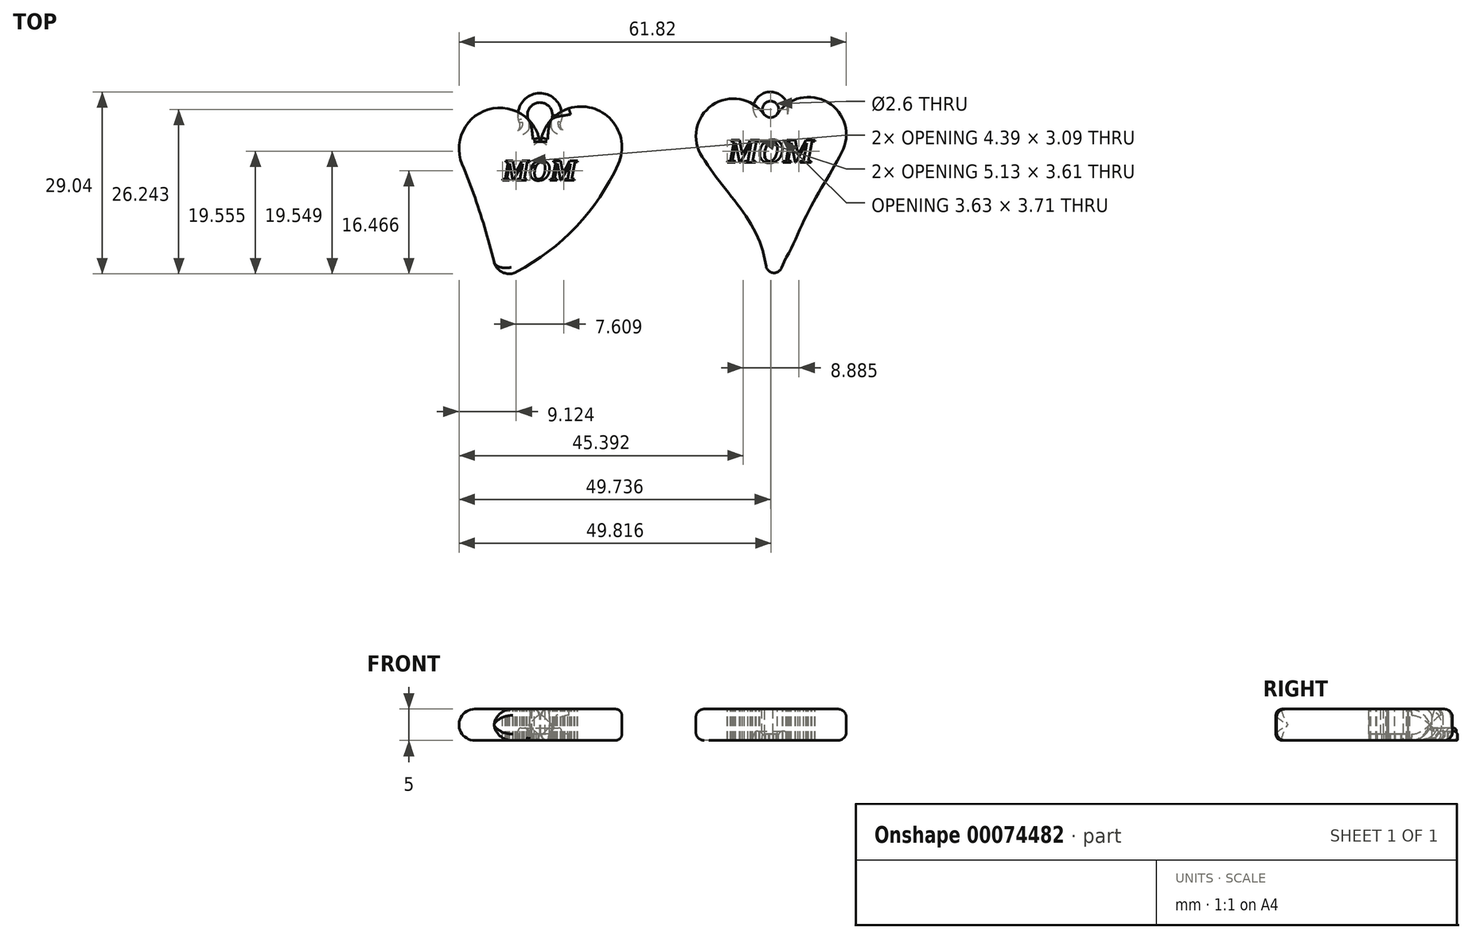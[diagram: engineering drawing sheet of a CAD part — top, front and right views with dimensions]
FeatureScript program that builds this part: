
annotation { "Feature Type Name" : "Feature", "Feature Type Description" : "" }
export const myFeature = defineFeature(function(context is Context, id is Id, definition is map)
    precondition{}
    {
        {
            var Q0;
            Q0=qCreatedBy(makeId("Top.planeOp"),FACE);
            var sketch = newSketch(context, id + "F0", { "sketchPlane" : qUnion([Q0])});
            skLineSegment(sketch, "E0.rect.bottom", {"start": v(-16, 20) * mm, "end": v(16, 20) * mm, "construction": true});
            skLineSegment(sketch, "E0.rect.top", {"start": v(-16, -20) * mm, "end": v(16, -20) * mm, "construction": true});
            skLineSegment(sketch, "E0.rect.left", {"start": v(-16, 20) * mm, "end": v(-16, -20) * mm, "construction": true});
            skLineSegment(sketch, "E0.rect.right", {"start": v(16, 20) * mm, "end": v(16, -20) * mm, "construction": true});
            skLineSegment(sketch, "E1", {"start": v(0, 0) * mm, "end": v(0, 20) * mm, "construction": true});
            skCircle(sketch, "E2", {"center": v(-6, 8.56) * mm, "radius": 6 * mm});
            skCircle(sketch, "E3", {"center": v(6, 8.8) * mm, "radius": 6 * mm});
            skFitSpline(sketch, "E4", {"points": [v(-11, 5.26) * mm, v(-8.06, 1.11) * mm, v(-4.05, -4.17) * mm, v(-1.25, -10.02) * mm, v(0, -13.64) * mm, v(2.4, -10.88) * mm, v(4.4, -6.78) * mm, v(5.94, -3.48) * mm, v(7.87, 0) * mm, v(8.52, 1.1) * mm, v(12.07, 7.48) * mm], "startDerivative": vector(36.89, -55.96) * mm, "endDerivative": vector(45.04, 87.27) * mm});
            skLineSegment(sketch, "E5", {"start": v(6, 8.8) * mm, "end": v(12, 8.8) * mm});
            skLineSegment(sketch, "E6", {"start": v(-1.28, -9.88) * mm, "end": v(0, -16.13) * mm});
            skLineSegment(sketch, "E7", {"start": v(0, -16.13) * mm, "end": v(2.4, -10.88) * mm});
            skSolve(sketch);
        }
        {
            var Q0;
            Q0 = qSketchRegion(id + "F0", true);
            extrude(context, id + "F1", {"entities" : qUnion([Q0]), "depth" : 5 * mm});
        }
        {
            var Q0;
            Q0=qCreatedBy(makeId("Top.planeOp"),FACE);
            var sketch = newSketch(context, id + "F2", { "sketchPlane" : qUnion([Q0])});
            skCircle(sketch, "E8", {"center": v(-43.32, 6.6) * mm, "radius": 6.5 * mm});
            skCircle(sketch, "E9", {"center": v(-30.32, 6.8) * mm, "radius": 6.5 * mm});
            skArc(sketch, "E10", {"start": v(-43.55, -14.49) * mm, "mid": v(-46.01, -5.06) * mm, "end": v(-49.32, 4.1) * mm});
            skArc(sketch, "E11", {"start": v(-43.55, -14.49) * mm, "mid": v(-32.21, -7) * mm, "end": v(-24.4, 4.1) * mm});
            skSolve(sketch);
        }
        {
            var Q0;
            {var subQ0=sQuery(id+"F2.wireOp",EDGE,"E10");Q0=makeQuery(id+"F2.imprint","IMPRINT",FACE,{"disambiguationData":[TD([[makeQuery(id+"F2.imprint","IMPRINT",EDGE,{"derivedFrom":subQ0}),-1.0]])]});}
            var Q1;
            {var subQ0=sQuery(id+"F2.wireOp",EDGE,"E8");var subQ1=makeQuery(id+"F2.imprint","INTERSECT",VERTEX,{"derivedFrom":[subQ0,sQuery(id+"F2.wireOp",EDGE,"E10")]});Q1=makeQuery(id+"F2.imprint","IMPRINT",FACE,{"disambiguationData":[TD([[makeQuery(id+"F2.imprint","IMPRINT",EDGE,{"disambiguationData":[TD([[subQ1,1.0]])],"derivedFrom":subQ0}),1.0]])]});}
            var Q2;
            {var subQ0=sQuery(id+"F2.wireOp",EDGE,"E9");var subQ1=makeQuery(id+"F2.imprint","INTERSECT",VERTEX,{"derivedFrom":[subQ0,sQuery(id+"F2.wireOp",EDGE,"E11")]});Q2=makeQuery(id+"F2.imprint","IMPRINT",FACE,{"disambiguationData":[TD([[makeQuery(id+"F2.imprint","IMPRINT",EDGE,{"disambiguationData":[TD([[subQ1,1.0]])],"derivedFrom":subQ0}),1.0]])]});}
            extrude(context, id + "F3", {"entities" : qUnion([Q0, Q1, Q2]), "depth" : 5 * mm});
        }
        {
            var Q0;
            Q0=makeQuery(id+"F3.opExtrude","SWEPT_FACE",FACE,{"disambiguationData":[OSD([sQuery(id+"F2.wireOp",EDGE,"E10")])]});
            var Q1;
            Q1=makeQuery(id+"F3.opExtrude","SWEPT_FACE",FACE,{"disambiguationData":[OSD([sQuery(id+"F2.wireOp",EDGE,"E8")])]});
            fillet(context, id + "F4", {"entities" : qUnion([Q0, Q1]), "radius" : 2.5 * mm, "tangentPropagation" : true, "allowEdgeOverflow" : false});
        }
        {
            var Q0;
            Q0=makeQuery(id+"F3.opExtrude","CAP_FACE",FACE,{"disambiguationData":[OSD([sQuery(id+"F2.wireOp",EDGE,"E8"),sQuery(id+"F2.wireOp",EDGE,"E9"),sQuery(id+"F2.wireOp",EDGE,"E10"),sQuery(id+"F2.wireOp",EDGE,"E11")])],"isStart":false});
            var sketch = newSketch(context, id + "F5", { "sketchPlane" : qUnion([Q0])});
            skArc(sketch, "E12", {"start": v(-43.41, 13.1) * mm, "mid": v(-48.75, 10.17) * mm, "end": v(-49.32, 4.1) * mm});
            skArc(sketch, "E13", {"start": v(-24.85, 3.27) * mm, "mid": v(-24.63, 9.95) * mm, "end": v(-30.42, 13.3) * mm});
            skCircle(sketch, "E14", {"center": v(-43.32, 6.6) * mm, "radius": 6.5 * mm});
            skCircle(sketch, "E15", {"center": v(-30.32, 6.8) * mm, "radius": 6.5 * mm});
            skLineSegment(sketch, "E16", {"start": v(-43.41, 13.1) * mm, "end": v(-30.42, 13.3) * mm});
            skLineSegment(sketch, "E17", {"start": v(-36.9, 7.67) * mm, "end": v(-36.76, 7.67) * mm});
            skSolve(sketch);
        }
        {
            var Q0;
            {var subQ0=sQuery(id+"F5.wireOp",EDGE,"E16");Q0=makeQuery(id+"F5.imprint","IMPRINT",FACE,{"disambiguationData":[TD([[makeQuery(id+"F5.imprint","IMPRINT",EDGE,{"derivedFrom":subQ0}),-1.0]])]});}
            var Q1;
            {var subQ0=sQuery(id+"F5.wireOp",EDGE,"E17");Q1=makeQuery(id+"F5.imprint","IMPRINT",FACE,{"disambiguationData":[TD([[makeQuery(id+"F5.imprint","IMPRINT",EDGE,{"derivedFrom":subQ0}),1.0]])]});}
            extrude(context, id + "F6", {"entities" : qUnion([Q0, Q1]), "operationType" : NewBodyOperationType.REMOVE, "oppositeDirection" : true, "depth" : 25 * mm});
        }
        {
            var Q0;
            Q0=makeQuery(id+"F6.boolean.opBoolean","INTERSECT",EDGE,{"disambiguationData":[OD(0.0)],"derivedFrom":[makeQuery(id+"F4.opFillet","BLEND_FACE",FACE,{"disambiguationData":[OSD([sQuery(id+"F2.wireOp",EDGE,"E8"),sQuery(id+"F2.wireOp",EDGE,"E9")])]}),makeQuery(id+"F6.opExtrude","SWEPT_FACE",FACE,{"disambiguationData":[OSD([sQuery(id+"F5.wireOp",EDGE,"E15")])]})]});
            var Q1;
            Q1=makeQuery(id+"F6.boolean.opBoolean","INTERSECT",EDGE,{"disambiguationData":[OD(1.0)],"derivedFrom":[makeQuery(id+"F4.opFillet","BLEND_FACE",FACE,{"disambiguationData":[OSD([sQuery(id+"F2.wireOp",EDGE,"E8"),sQuery(id+"F2.wireOp",EDGE,"E9")])]}),makeQuery(id+"F6.opExtrude","SWEPT_FACE",FACE,{"disambiguationData":[OSD([sQuery(id+"F5.wireOp",EDGE,"E15")])]})]});
            var Q2;
            Q2=makeQuery(id+"F6.boolean.opBoolean","INTERSECT",EDGE,{"disambiguationData":[OD(1.0)],"derivedFrom":[makeQuery(id+"F4.opFillet","BLEND_FACE",FACE,{"disambiguationData":[OSD([sQuery(id+"F2.wireOp",EDGE,"E8"),sQuery(id+"F2.wireOp",EDGE,"E9")])]}),makeQuery(id+"F6.opExtrude","SWEPT_FACE",FACE,{"disambiguationData":[OSD([sQuery(id+"F5.wireOp",EDGE,"E14")])]})]});
            var Q3;
            Q3=makeQuery(id+"F6.boolean.opBoolean","INTERSECT",EDGE,{"disambiguationData":[OD(0.0)],"derivedFrom":[makeQuery(id+"F4.opFillet","BLEND_FACE",FACE,{"disambiguationData":[OSD([sQuery(id+"F2.wireOp",EDGE,"E8"),sQuery(id+"F2.wireOp",EDGE,"E9")])]}),makeQuery(id+"F6.opExtrude","SWEPT_FACE",FACE,{"disambiguationData":[OSD([sQuery(id+"F5.wireOp",EDGE,"E14")])]})]});
            var Q4;
            {var subQ0=sQuery(id+"F2.wireOp",EDGE,"E11");var subQ1=sQuery(id+"F2.wireOp",EDGE,"E10");var subQ2=sQuery(id+"F2.wireOp",EDGE,"E9");var subQ3=sQuery(id+"F2.wireOp",EDGE,"E8");Q4=makeQuery(id+"F6.boolean.opBoolean","MERGE",EDGE,{"derivedFrom":[makeQuery(id+"F4.opFillet","BLEND_EDGE",EDGE,{"blendedFrom":[makeQuery(id+"F3.opExtrude","CAP_VERTEX",VERTEX,{"disambiguationData":[OSD([subQ3,subQ2])],"isStart":false}),makeQuery(id+"F3.opExtrude","CAP_FACE",FACE,{"disambiguationData":[OSD([subQ3,subQ2,subQ1,subQ0])],"isStart":false})],"blendedInto":[makeQuery(id+"F3.opExtrude","CAP_FACE",FACE,{"disambiguationData":[OSD([subQ3,subQ2,subQ1,subQ0])],"isStart":false})]}),makeQuery(id+"F6.opExtrude","CAP_EDGE",EDGE,{"disambiguationData":[OSD([subQ3,subQ2,subQ1,subQ0])],"isStart":true})]});}
            fillet(context, id + "F7", {"entities" : qUnion([Q0, Q1, Q2, Q3, Q4]), "radius" : 1 * mm, "tangentPropagation" : true, "allowEdgeOverflow" : false});
        }
        {
            var Q0;
            Q0=makeQuery(id+"F3.opExtrude","CAP_FACE",FACE,{"disambiguationData":[OSD([sQuery(id+"F2.wireOp",EDGE,"E8"),sQuery(id+"F2.wireOp",EDGE,"E9"),sQuery(id+"F2.wireOp",EDGE,"E10"),sQuery(id+"F2.wireOp",EDGE,"E11")])],"isStart":true});
            var sketch = newSketch(context, id + "F8", { "sketchPlane" : qUnion([Q0])});
            skArc(sketch, "E18", {"start": v(-35, -11.3) * mm, "mid": v(-26.28, -11.89) * mm, "end": v(-24.85, -3.27) * mm});
            skArc(sketch, "E19", {"start": v(-49.32, -4.1) * mm, "mid": v(-46.96, -11.98) * mm, "end": v(-38.77, -11.24) * mm});
            skArc(sketch, "E20", {"start": v(-38.77, -11.24) * mm, "mid": v(-36.93, -13.93) * mm, "end": v(-35, -11.3) * mm});
            skArc(sketch, "E21.0", {"start": v(-40.18, -10.73) * mm, "mid": v(-36.95, -15.43) * mm, "end": v(-33.58, -10.83) * mm});
            skArc(sketch, "E22", {"start": v(-33.25, -9.51) * mm, "mid": v(-33.6, -10.12) * mm, "end": v(-33.58, -10.83) * mm});
            skArc(sketch, "E23", {"start": v(-34.43, -8.58) * mm, "mid": v(-35.08, -9.86) * mm, "end": v(-35, -11.3) * mm});
            skArc(sketch, "E24", {"start": v(-38.77, -11.24) * mm, "mid": v(-38.65, -9.8) * mm, "end": v(-39.26, -8.5) * mm});
            skArc(sketch, "E25", {"start": v(-40.18, -10.73) * mm, "mid": v(-40.13, -10.02) * mm, "end": v(-40.47, -9.4) * mm});
            skSolve(sketch);
        }
        {
            var Q0;
            {var subQ0=sQuery(id+"F8.wireOp",EDGE,"E20");Q0=makeQuery(id+"F8.imprint","IMPRINT",FACE,{"disambiguationData":[TD([[makeQuery(id+"F8.imprint","IMPRINT",EDGE,{"derivedFrom":subQ0}),-1.0]])]});}
            var Q1;
            {var subQ1=sQuery(id+"F8.wireOp",EDGE,"E22");Q1=makeQuery(id+"F8.imprint","IMPRINT",FACE,{"disambiguationData":[TD([[makeQuery(id+"F8.imprint","IMPRINT",EDGE,{"derivedFrom":subQ1}),-1.0]])]});}
            var Q2;
            {var subQ1=sQuery(id+"F8.wireOp",EDGE,"E24");Q2=makeQuery(id+"F8.imprint","IMPRINT",FACE,{"disambiguationData":[TD([[makeQuery(id+"F8.imprint","IMPRINT",EDGE,{"derivedFrom":subQ1}),1.0]])]});}
            extrude(context, id + "F9", {"entities" : qUnion([Q0, Q1, Q2]), "operationType" : NewBodyOperationType.ADD, "oppositeDirection" : true, "depth" : 2 * mm});
        }
        {
            var Q0;
            Q0=makeQuery(id+"F9.opExtrude","CAP_EDGE",EDGE,{"disambiguationData":[OSD([sQuery(id+"F8.wireOp",EDGE,"E20")])],"isStart":true});
            var Q1;
            Q1=makeQuery(id+"F9.opExtrude","CAP_EDGE",EDGE,{"disambiguationData":[OSD([sQuery(id+"F8.wireOp",EDGE,"E21.0")])],"isStart":true});
            var Q2;
            Q2=makeQuery(id+"F9.opExtrude","CAP_EDGE",EDGE,{"disambiguationData":[OSD([sQuery(id+"F8.wireOp",EDGE,"E21.0")])],"isStart":false});
            var Q3;
            Q3=makeQuery(id+"F9.opExtrude","CAP_EDGE",EDGE,{"disambiguationData":[OSD([sQuery(id+"F8.wireOp",EDGE,"E20")])],"isStart":false});
            var Q4;
            {var subQ0=sQuery(id+"F2.wireOp",EDGE,"E9");var subQ1=sQuery(id+"F2.wireOp",EDGE,"E8");var subQ2=sQuery(id+"F2.wireOp",EDGE,"E11");var subQ3=sQuery(id+"F2.wireOp",EDGE,"E10");var subQ4=makeQuery(id+"F3.opExtrude","CAP_FACE",FACE,{"disambiguationData":[OSD([subQ1,subQ0,subQ3,subQ2])],"isStart":true});Q4=makeQuery(id+"F6.boolean.opBoolean","SPLIT",EDGE,{"disambiguationData":[TD([subQ4,makeQuery(id+"F4.opFillet","BLEND_FACE",FACE,{"disambiguationData":[OSD([subQ1,subQ0])]}),makeQuery(id+"F6.opExtrude","SWEPT_FACE",FACE,{"disambiguationData":[OSD([sQuery(id+"F5.wireOp",EDGE,"E14")])]}),makeQuery(id+"F6.opExtrude","SWEPT_FACE",FACE,{"disambiguationData":[OSD([sQuery(id+"F5.wireOp",EDGE,"E15")])]}),makeQuery(id+"F6.opExtrude","SWEPT_FACE",FACE,{"disambiguationData":[OSD([subQ1,subQ0,subQ3,subQ2])]})])],"derivedFrom":makeQuery(id+"F4.opFillet","BLEND_EDGE",EDGE,{"blendedFrom":[makeQuery(id+"F3.opExtrude","CAP_VERTEX",VERTEX,{"disambiguationData":[OSD([subQ1,subQ0])],"isStart":true}),subQ4],"blendedInto":[subQ4]})});}
            fillet(context, id + "F10", {"entities" : qUnion([Q0, Q1, Q2, Q3, Q4]), "radius" : .5 * mm, "tangentPropagation" : true, "allowEdgeOverflow" : false});
        }
        {
            var Q0;
            Q0=makeQuery(id+"F3.opExtrude","CAP_FACE",FACE,{"disambiguationData":[OSD([sQuery(id+"F2.wireOp",EDGE,"E8"),sQuery(id+"F2.wireOp",EDGE,"E9"),sQuery(id+"F2.wireOp",EDGE,"E10"),sQuery(id+"F2.wireOp",EDGE,"E11")])],"isStart":false});
            var sketch = newSketch(context, id + "F11", { "sketchPlane" : qUnion([Q0])});
            skText(sketch, "E26", { "text": "MOM", "fontName": "Tinos-BoldItalic.ttf"});
            const initialGuessF11  = {"E26": [-0.04283, 0.00152, 1, 0, 0.0034]};
            skSetInitialGuess(sketch, initialGuessF11);
            skSolve(sketch);
        }
        {
            var Q0;
            Q0 = qSketchRegion(id + "F11", true);
            extrude(context, id + "F12", {"entities" : qUnion([Q0]), "operationType" : NewBodyOperationType.REMOVE, "oppositeDirection" : true, "depth" : 25 * mm});
        }
        {
            var Q0;
            {var subQ0=sQuery(id+"F2.wireOp",EDGE,"E8");var subQ1=sQuery(id+"F2.wireOp",EDGE,"E9");var subQ2=sQuery(id+"F8.wireOp",EDGE,"E24");var subQ3=sQuery(id+"F2.wireOp",EDGE,"E11");var subQ6=sQuery(id+"F8.wireOp",EDGE,"E23");var subQ7=sQuery(id+"F2.wireOp",EDGE,"E10");var subQ8=sQuery(id+"F8.wireOp",EDGE,"E20");var subQ9=sQuery(id+"F8.wireOp",EDGE,"E21.0");var subQ12=sQuery(id+"F8.wireOp",EDGE,"E22");var subQ13=sQuery(id+"F8.wireOp",EDGE,"E25");Q0=makeQuery(id+"F12.boolean.opBoolean","SPLIT",FACE,{"disambiguationData":[TD([makeQuery(id+"F4.opFillet","BLEND_FACE",FACE,{"disambiguationData":[OSD([subQ0])]})])],"derivedFrom":makeQuery(id+"F9.boolean.opBoolean","MERGE",FACE,{"derivedFrom":[makeQuery(id+"F3.opExtrude","CAP_FACE",FACE,{"disambiguationData":[OSD([subQ0,subQ1,subQ7,subQ3])],"isStart":true}),makeQuery(id+"F9.opExtrude","CAP_FACE",FACE,{"disambiguationData":[OSD([subQ0,subQ1,subQ7,subQ3,subQ8,subQ9,subQ12,subQ6,subQ2,subQ13])],"isStart":true})]})});}
            var sketch = newSketch(context, id + "F13", { "sketchPlane" : qUnion([Q0])});
            skFitSpline(sketch, "E27.0.0", {"points": [v(-37.04, -3.52) * mm, v(-36.86, -3.27) * mm, v(-36.86, -2.84) * mm]});
            skFitSpline(sketch, "E27.0.1", {"points": [v(-36.86, -2.84) * mm, v(-36.86, -2.4) * mm, v(-37.01, -1.97) * mm]});
            skFitSpline(sketch, "E27.0.2", {"points": [v(-37.01, -1.97) * mm, v(-37.17, -1.54) * mm, v(-37.4, -1.31) * mm]});
            skFitSpline(sketch, "E27.0.3", {"points": [v(-37.4, -1.31) * mm, v(-37.64, -1.08) * mm, v(-37.93, -1.08) * mm]});
            skFitSpline(sketch, "E27.0.4", {"points": [v(-37.93, -1.08) * mm, v(-38.24, -1.08) * mm, v(-38.4, -1.33) * mm]});
            skFitSpline(sketch, "E27.0.5", {"points": [v(-38.4, -1.33) * mm, v(-38.58, -1.58) * mm, v(-38.58, -2.01) * mm]});
            skFitSpline(sketch, "E27.0.6", {"points": [v(-38.58, -2.01) * mm, v(-38.58, -2.44) * mm, v(-38.43, -2.88) * mm]});
            skFitSpline(sketch, "E27.0.7", {"points": [v(-38.43, -2.88) * mm, v(-38.28, -3.31) * mm, v(-38.04, -3.55) * mm]});
            skFitSpline(sketch, "E27.0.8", {"points": [v(-38.04, -3.55) * mm, v(-37.8, -3.78) * mm, v(-37.53, -3.78) * mm]});
            skFitSpline(sketch, "E27.0.9", {"points": [v(-37.53, -3.78) * mm, v(-37.21, -3.78) * mm, v(-37.04, -3.52) * mm]});
            skLineSegment(sketch, "E28", {"start": v(-37.62, -3.5) * mm, "end": v(-38.33, -3.5) * mm});
            skLineSegment(sketch, "E29", {"start": v(-37.77, -2.64) * mm, "end": v(-38.46, -2.64) * mm});
            skLineSegment(sketch, "E30", {"start": v(-36.05, -3.46) * mm, "end": v(-35.36, -3.46) * mm});
            skLineSegment(sketch, "E31", {"start": v(-36.2, -2.6) * mm, "end": v(-35.5, -2.6) * mm});
            skFitSpline(sketch, "E32.0", {"points": [v(-36.17, -2.76) * mm, v(-36.17, -2.21) * mm, v(-36.4, -1.76) * mm]});
            skFitSpline(sketch, "E33.0", {"points": [v(-36.33, -3.42) * mm, v(-36.17, -3.13) * mm, v(-36.17, -2.76) * mm]});
            skFitSpline(sketch, "E34.0", {"points": [v(-39.27, -2.1) * mm, v(-39.27, -2.66) * mm, v(-39.05, -3.1) * mm]});
            skFitSpline(sketch, "E35.0", {"points": [v(-39.11, -1.45) * mm, v(-39.27, -1.74) * mm, v(-39.27, -2.1) * mm]});
            skSolve(sketch);
        }
        {
            var Q0;
            Q0=makeQuery(id+"F13.imprint","IMPRINT",FACE,{"disambiguationData":[TD([[makeQuery(id+"F13.imprint","IMPRINT",EDGE,{"derivedFrom":sQuery(id+"F13.wireOp",EDGE,"E27.0.1")}),-1.0]])]});
            var Q1;
            Q1=makeQuery(id+"F13.imprint","IMPRINT",FACE,{"disambiguationData":[TD([[makeQuery(id+"F13.imprint","IMPRINT",EDGE,{"derivedFrom":sQuery(id+"F13.wireOp",EDGE,"E27.0.6")}),-1.0]])]});
            extrude(context, id + "F14", {"entities" : qUnion([Q0, Q1]), "operationType" : NewBodyOperationType.ADD, "oppositeDirection" : true, "depth" : 1 * mm});
        }
        {
            var Q0;
            Q0=makeQuery(id+"F1.opExtrude","SWEPT_FACE",FACE,{"disambiguationData":[OSD([sQuery(id+"F0.wireOp",EDGE,"E2")])]});
            var Q1;
            Q1=makeQuery(id+"F1.opExtrude","SWEPT_FACE",FACE,{"disambiguationData":[OSD([sQuery(id+"F0.wireOp",EDGE,"E6")])]});
            var Q2;
            {var subQ0=sQuery(id+"F0.wireOp",EDGE,"E4");Q2=makeQuery(id+"F1.opExtrude","SWEPT_FACE",FACE,{"disambiguationData":[OSD([subQ0]),TDD([makeQuery(id+"F0.imprint","IMPRINT",EDGE,{"disambiguationData":[TD([[makeQuery(id+"F0.imprint","INTERSECT",VERTEX,{"derivedFrom":[sQuery(id+"F0.wireOp",EDGE,"E2"),subQ0]}),-1.0]])],"derivedFrom":subQ0})])]});}
            var Q3;
            Q3=makeQuery(id+"F1.opExtrude","SWEPT_FACE",FACE,{"disambiguationData":[OSD([sQuery(id+"F0.wireOp",EDGE,"E3")])]});
            var Q4;
            {var subQ0=sQuery(id+"F0.wireOp",EDGE,"E4");Q4=makeQuery(id+"F1.opExtrude","SWEPT_FACE",FACE,{"disambiguationData":[OSD([subQ0]),TDD([makeQuery(id+"F0.imprint","IMPRINT",EDGE,{"disambiguationData":[TD([[makeQuery(id+"F0.imprint","INTERSECT",VERTEX,{"derivedFrom":[sQuery(id+"F0.wireOp",EDGE,"E3"),subQ0]}),1.0]])],"derivedFrom":subQ0})])]});}
            var Q5;
            Q5=makeQuery(id+"F1.opExtrude","SWEPT_FACE",FACE,{"disambiguationData":[OSD([sQuery(id+"F0.wireOp",EDGE,"E7")])]});
            fillet(context, id + "F15", {"entities" : qUnion([Q0, Q1, Q2, Q3, Q4, Q5]), "radius" : 1.3 * mm, "tangentPropagation" : true, "allowEdgeOverflow" : false});
        }
        {
            var Q0;
            Q0=makeQuery(id+"F6.boolean.opBoolean","COPY",EDGE,{"derivedFrom":makeQuery(id+"F6.opExtrude","CAP_EDGE",EDGE,{"disambiguationData":[OSD([sQuery(id+"F5.wireOp",EDGE,"E17")])],"isStart":true})});
            var Q1;
            Q1=makeQuery(id+"F6.boolean.opBoolean","INTERSECT",EDGE,{"derivedFrom":[makeQuery(id+"F3.opExtrude","CAP_FACE",FACE,{"disambiguationData":[OSD([sQuery(id+"F2.wireOp",EDGE,"E8"),sQuery(id+"F2.wireOp",EDGE,"E9"),sQuery(id+"F2.wireOp",EDGE,"E10"),sQuery(id+"F2.wireOp",EDGE,"E11")])],"isStart":true}),makeQuery(id+"F6.opExtrude","SWEPT_FACE",FACE,{"disambiguationData":[OSD([sQuery(id+"F5.wireOp",EDGE,"E17")])]})]});
            fillet(context, id + "F16", {"entities" : qUnion([Q0, Q1]), "radius" : .5 * mm, "tangentPropagation" : true, "allowEdgeOverflow" : false});
        }
        {
            var Q0;
            Q0=makeQuery(id+"F1.opExtrude","CAP_FACE",FACE,{"disambiguationData":[OSD([sQuery(id+"F0.wireOp",EDGE,"E2"),sQuery(id+"F0.wireOp",EDGE,"E3"),sQuery(id+"F0.wireOp",EDGE,"E4"),sQuery(id+"F0.wireOp",EDGE,"E6"),sQuery(id+"F0.wireOp",EDGE,"E7")])],"isStart":true});
            var sketch = newSketch(context, id + "F17", { "sketchPlane" : qUnion([Q0])});
            skArc(sketch, "E36.0", {"start": v(1, -12.12) * mm, "mid": v(-0.06, -11.54) * mm, "end": v(-1.14, -12.08) * mm});
            skArc(sketch, "E37.0", {"start": v(2.08, -11.4) * mm, "mid": v(8.4, -12.85) * mm, "end": v(10.15, -6.6) * mm});
            skArc(sketch, "E38.0", {"start": v(-9.92, -5.98) * mm, "mid": v(-8.67, -12.43) * mm, "end": v(-2.19, -11.32) * mm});
            skArc(sketch, "E39.0", {"start": v(-2.19, -11.32) * mm, "mid": v(-0.03, -10.24) * mm, "end": v(2.08, -11.4) * mm});
            skCircle(sketch, "E40", {"center": v(-0.08, -12.84) * mm, "radius": 1.3 * mm});
            skCircle(sketch, "E41.0", {"center": v(-0.08, -12.84) * mm, "radius": 2.8 * mm});
            skSolve(sketch);
        }
        {
            var Q0;
            {var subQ3=sQuery(id+"F17.wireOp",EDGE,"E39.0");Q0=makeQuery(id+"F17.imprint","IMPRINT",FACE,{"disambiguationData":[TD([[makeQuery(id+"F17.imprint","IMPRINT",EDGE,{"derivedFrom":subQ3}),-1.0]])]});}
            var Q1;
            {var subQ0=sQuery(id+"F17.wireOp",EDGE,"E39.0");Q1=makeQuery(id+"F17.imprint","IMPRINT",FACE,{"disambiguationData":[TD([[makeQuery(id+"F17.imprint","IMPRINT",EDGE,{"derivedFrom":subQ0}),1.0]])]});}
            extrude(context, id + "F18", {"entities" : qUnion([Q0, Q1]), "operationType" : NewBodyOperationType.ADD, "oppositeDirection" : true, "depth" : 1.5 * mm});
        }
        {
            var Q0;
            Q0=makeQuery(id+"F18.opExtrude","CAP_EDGE",EDGE,{"disambiguationData":[OSD([sQuery(id+"F17.wireOp",EDGE,"E41.0")])],"isStart":true});
            var Q1;
            Q1=makeQuery(id+"F18.opExtrude","CAP_EDGE",EDGE,{"disambiguationData":[OSD([sQuery(id+"F17.wireOp",EDGE,"E40")])],"isStart":true});
            fillet(context, id + "F19", {"entities" : qUnion([Q0, Q1]), "radius" : .2 * mm, "tangentPropagation" : true, "allowEdgeOverflow" : false});
        }
        {
            var Q0;
            Q0=makeQuery(id+"F18.opExtrude","CAP_EDGE",EDGE,{"disambiguationData":[OSD([sQuery(id+"F17.wireOp",EDGE,"E41.0")])],"isStart":false});
            var Q1;
            Q1=makeQuery(id+"F18.opExtrude","CAP_EDGE",EDGE,{"disambiguationData":[OSD([sQuery(id+"F17.wireOp",EDGE,"E40")])],"isStart":false});
            fillet(context, id + "F20", {"entities" : qUnion([Q0, Q1]), "radius" : .75 * mm, "tangentPropagation" : true, "allowEdgeOverflow" : false});
        }
        {
            var Q0;
            Q0=makeQuery(id+"F1.opExtrude","CAP_FACE",FACE,{"disambiguationData":[OSD([sQuery(id+"F0.wireOp",EDGE,"E2"),sQuery(id+"F0.wireOp",EDGE,"E3"),sQuery(id+"F0.wireOp",EDGE,"E4"),sQuery(id+"F0.wireOp",EDGE,"E6"),sQuery(id+"F0.wireOp",EDGE,"E7")])],"isStart":false});
            var sketch = newSketch(context, id + "F21", { "sketchPlane" : qUnion([Q0])});
            skText(sketch, "E42", { "text": "MOM", "fontName": "Tinos-BoldItalic.ttf"});
            const initialGuessF21  = {"E42": [-0.00692, 0.00435, 1, 0, 0.00397]};
            skSetInitialGuess(sketch, initialGuessF21);
            skSolve(sketch);
        }
        {
            var Q0;
            Q0 = qSketchRegion(id + "F21", true);
            extrude(context, id + "F22", {"entities" : qUnion([Q0]), "operationType" : NewBodyOperationType.REMOVE, "oppositeDirection" : true, "depth" : 25 * mm});
        }
        {
            var Q0;
            {var subQ0=sQuery(id+"F0.wireOp",EDGE,"E7");var subQ1=sQuery(id+"F0.wireOp",EDGE,"E6");var subQ2=sQuery(id+"F0.wireOp",EDGE,"E3");var subQ3=sQuery(id+"F0.wireOp",EDGE,"E4");var subQ4=sQuery(id+"F0.wireOp",EDGE,"E2");var subQ5=sQuery(id+"F17.wireOp",EDGE,"E40");var subQ6=sQuery(id+"F17.wireOp",EDGE,"E41.0");Q0=makeQuery(id+"F22.boolean.opBoolean","SPLIT",FACE,{"disambiguationData":[TD([makeQuery(id+"F19.opFillet","BLEND_FACE",FACE,{"disambiguationData":[OSD([subQ5])]})])],"derivedFrom":makeQuery(id+"F18.boolean.opBoolean","MERGE",FACE,{"derivedFrom":[makeQuery(id+"F1.opExtrude","CAP_FACE",FACE,{"disambiguationData":[OSD([subQ4,subQ2,subQ3,subQ1,subQ0])],"isStart":true}),makeQuery(id+"F18.opExtrude","CAP_FACE",FACE,{"disambiguationData":[OSD([subQ5,subQ6])],"isStart":true})]})});}
            var sketch = newSketch(context, id + "F23", { "sketchPlane" : qUnion([Q0])});
            skFitSpline(sketch, "E43.0.0", {"points": [v(0.78, -7.42) * mm, v(0.99, -7.13) * mm, v(0.99, -6.62) * mm]});
            skFitSpline(sketch, "E43.0.1", {"points": [v(0.99, -6.62) * mm, v(0.99, -6.1) * mm, v(0.81, -5.6) * mm]});
            skFitSpline(sketch, "E43.0.2", {"points": [v(0.81, -5.6) * mm, v(0.63, -5.1) * mm, v(0.36, -4.84) * mm]});
            skFitSpline(sketch, "E43.0.3", {"points": [v(0.36, -4.84) * mm, v(0.08, -4.58) * mm, v(-0.26, -4.58) * mm]});
            skFitSpline(sketch, "E43.0.4", {"points": [v(-0.26, -4.58) * mm, v(-0.62, -4.58) * mm, v(-0.82, -4.86) * mm]});
            skFitSpline(sketch, "E43.0.5", {"points": [v(-0.82, -4.86) * mm, v(-1.01, -5.15) * mm, v(-1.01, -5.66) * mm]});
            skFitSpline(sketch, "E43.0.6", {"points": [v(-1.01, -5.66) * mm, v(-1.01, -6.16) * mm, v(-0.84, -6.67) * mm]});
            skFitSpline(sketch, "E43.0.7", {"points": [v(-0.84, -6.67) * mm, v(-0.67, -7.18) * mm, v(-0.39, -7.45) * mm]});
            skFitSpline(sketch, "E43.0.8", {"points": [v(-0.39, -7.45) * mm, v(-0.11, -7.72) * mm, v(0.21, -7.72) * mm]});
            skFitSpline(sketch, "E43.0.9", {"points": [v(0.21, -7.72) * mm, v(0.58, -7.72) * mm, v(0.78, -7.42) * mm]});
            skLineSegment(sketch, "E44", {"start": v(-0.84, -6.67) * mm, "end": v(-1.67, -6.67) * mm});
            skLineSegment(sketch, "E45", {"start": v(0.99, -6.62) * mm, "end": v(1.8, -6.62) * mm});
            skLineSegment(sketch, "E46", {"start": v(0.81, -5.6) * mm, "end": v(1.64, -5.6) * mm});
            skLineSegment(sketch, "E47", {"start": v(-1.01, -5.66) * mm, "end": v(-1.82, -5.66) * mm});
            skFitSpline(sketch, "E48.0", {"points": [v(1.8, -6.54) * mm, v(1.8, -5.9) * mm, v(1.53, -5.36) * mm]});
            skFitSpline(sketch, "E49.0", {"points": [v(1.6, -7.3) * mm, v(1.8, -6.96) * mm, v(1.8, -6.54) * mm]});
            skFitSpline(sketch, "E50.0", {"points": [v(-1.82, -5.76) * mm, v(-1.82, -6.41) * mm, v(-1.56, -6.93) * mm]});
            skFitSpline(sketch, "E51.0", {"points": [v(-1.63, -5) * mm, v(-1.82, -5.34) * mm, v(-1.82, -5.76) * mm]});
            skSolve(sketch);
        }
        {
            var Q0;
            Q0 = qSketchRegion(id + "F23", true);
            extrude(context, id + "F24", {"entities" : qUnion([Q0]), "operationType" : NewBodyOperationType.ADD, "oppositeDirection" : true, "depth" : 1 * mm});
        }
    });
